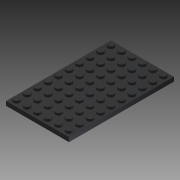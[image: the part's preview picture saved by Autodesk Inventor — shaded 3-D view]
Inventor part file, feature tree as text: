
AUTODESK INVENTOR PART (.ipt)
format: ipt  version: 2013 (Build 170138000, 138)  size: 305,152 bytes
history: native  units: mm
features: extrude x3, sketch x1, pattern_linear x1
ambient origin geometry x8: Origin, YZ Plane, XZ Plane, XY Plane, X Axis, Y Axis, Z Axis, Center Point
bodies: Solid1 (feature_tree)
feature tree (5):
  sketch  "Sketch1"  dims[d0=8.0mm d1=8.0mm d2=4.8mm d3=3.2mm d4=0.0mm d5=4.9mm d6=0.0mm d7=1.7mm d8=0.0mm d9=100.0mm d11=8.0mm d22=60.0mm d24=8.0mm]
  extrude  "Extrusion1"  Depth=8.0mm
  extrude  "Extrusion2"  Depth=4.8mm
  extrude  "Extrusion3"  Depth=3.2mm TaperAngle=0.0deg
  pattern_linear  "Rectangular Pattern1"  Spacing1=4.9mm  [1 undecoded]
note: 1 required parameter value undecoded (feature->parameter linkage not recoverable at this tier; creation-order binding heuristic only, values carry confidence <= 0.55)
